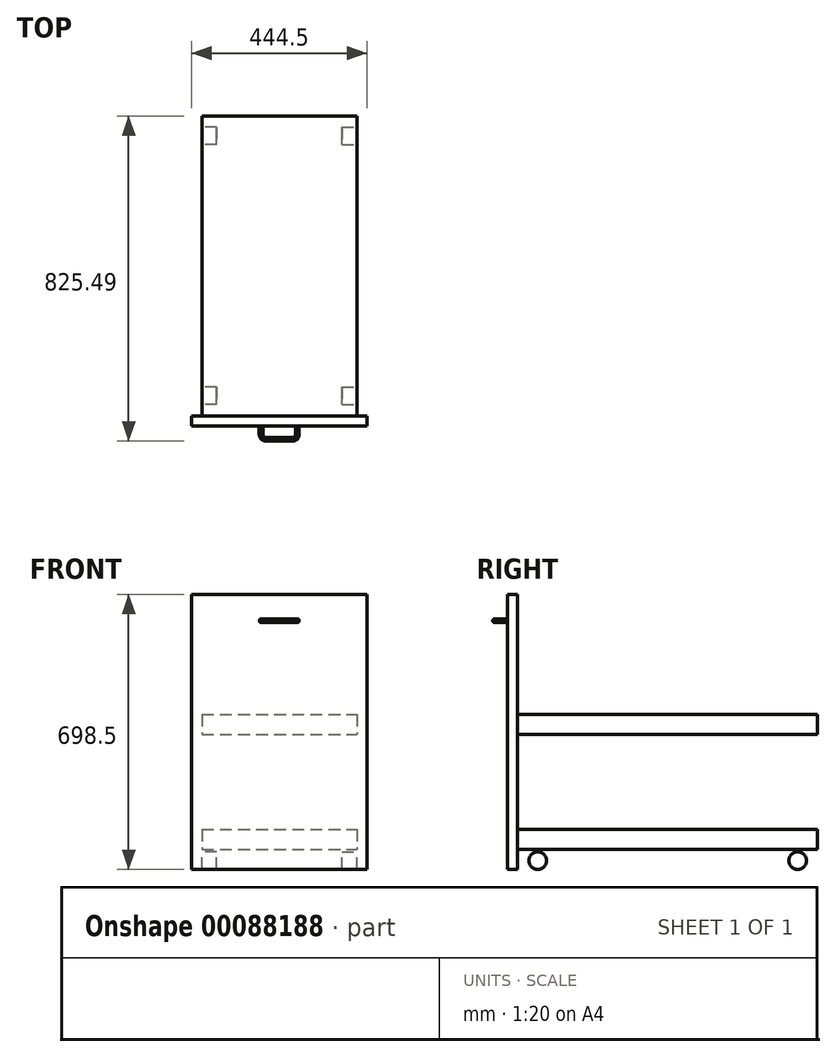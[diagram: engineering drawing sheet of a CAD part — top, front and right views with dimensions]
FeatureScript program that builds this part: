
annotation { "Feature Type Name" : "Feature", "Feature Type Description" : "" }
export const myFeature = defineFeature(function(context is Context, id is Id, definition is map)
    precondition{}
    {
        {
            var Q0;
            Q0=qCreatedBy(makeId("Front.planeOp"),FACE);
            var sketch = newSketch(context, id + "F0", { "sketchPlane" : qUnion([Q0])});
            skLineSegment(sketch, "E0.bottom", {"start": v(-222.25, 0) * mm, "end": v(222.25, 0) * mm});
            skLineSegment(sketch, "E0.top", {"start": v(-222.25, 698.5) * mm, "end": v(222.25, 698.5) * mm});
            skLineSegment(sketch, "E0.left", {"start": v(-222.25, 0) * mm, "end": v(-222.25, 698.5) * mm});
            skLineSegment(sketch, "E0.right", {"start": v(222.25, 0) * mm, "end": v(222.25, 698.5) * mm});
            skPoint(sketch, "E1", {"position": v(0, 0) * mm});
            skSolve(sketch);
        }
        {
            var Q0;
            Q0 = qSketchRegion(id + "F0", true);
            extrude(context, id + "F1", {"entities" : qUnion([Q0]), "depth" : 25.4 * mm});
        }
        {
            var Q0;
            Q0=makeQuery(id+"F1.opExtrude","CAP_FACE",FACE,{"disambiguationData":[OSD([sQuery(id+"F0.wireOp",EDGE,"E0.bottom"),sQuery(id+"F0.wireOp",EDGE,"E0.top"),sQuery(id+"F0.wireOp",EDGE,"E0.left"),sQuery(id+"F0.wireOp",EDGE,"E0.right")])],"isStart":true});
            var sketch = newSketch(context, id + "F2", { "sketchPlane" : qUnion([Q0])});
            skLineSegment(sketch, "E2.bottom", {"start": v(196.85, 393.7) * mm, "end": v(-196.85, 393.7) * mm});
            skLineSegment(sketch, "E2.top", {"start": v(196.85, 342.9) * mm, "end": v(-196.85, 342.9) * mm});
            skLineSegment(sketch, "E2.left", {"start": v(196.85, 393.7) * mm, "end": v(196.85, 342.9) * mm});
            skLineSegment(sketch, "E2.right", {"start": v(-196.85, 393.7) * mm, "end": v(-196.85, 342.9) * mm});
            skLineSegment(sketch, "E3.bottom", {"start": v(196.85, 101.6) * mm, "end": v(-196.85, 101.6) * mm});
            skLineSegment(sketch, "E3.top", {"start": v(196.85, 50.8) * mm, "end": v(-196.85, 50.8) * mm});
            skLineSegment(sketch, "E3.left", {"start": v(196.85, 101.6) * mm, "end": v(196.85, 50.8) * mm});
            skLineSegment(sketch, "E3.right", {"start": v(-196.85, 101.6) * mm, "end": v(-196.85, 50.8) * mm});
            skLineSegment(sketch, "E4", {"start": v(0, 698.5) * mm, "end": v(0, 393.7) * mm, "construction": true});
            skSolve(sketch);
        }
        {
            var Q0;
            Q0 = qSketchRegion(id + "F2", true);
            extrude(context, id + "F3", {"entities" : qUnion([Q0]), "operationType" : NewBodyOperationType.ADD, "depth" : 762 * mm});
        }
        {
            var Q0;
            Q0=makeQuery(id+"F3.opExtrude","SWEPT_FACE",FACE,{"disambiguationData":[OSD([sQuery(id+"F2.wireOp",EDGE,"E3.right")])]});
            var sketch = newSketch(context, id + "F4", { "sketchPlane" : qUnion([Q0])});
            skCircle(sketch, "E5", {"center": v(50.8, 22.22) * mm, "radius": 22.23 * mm});
            skCircle(sketch, "E6", {"center": v(711.2, 22.23) * mm, "radius": 22.23 * mm});
            skLineSegment(sketch, "E7", {"start": v(0, 0) * mm, "end": v(50.8, 0) * mm, "construction": true});
            skSolve(sketch);
        }
        {
            var Q0;
            Q0 = qSketchRegion(id + "F4", true);
            extrude(context, id + "F5", {"entities" : qUnion([Q0]), "oppositeDirection" : true, "depth" : 38.1 * mm});
        }
        {
            var Q0;
            Q0=makeQuery(id+"F5.opExtrude","SWEPT_BODY",BODY,{"disambiguationData":[OSD([sQuery(id+"F4.wireOp",EDGE,"E5")])]});
            var Q1;
            Q1=makeQuery(id+"F5.opExtrude","SWEPT_BODY",BODY,{"disambiguationData":[OSD([sQuery(id+"F4.wireOp",EDGE,"E6")])]});
            var Q2;
            Q2=qCreatedBy(makeId("Right.planeOp"),FACE);
            mirror(context, id + "F6", {"entities" : qUnion([Q0, Q1]), "mirrorPlane" : qUnion([Q2])});
        }
        {
            var Q0;
            Q0=qCreatedBy(makeId("Top.planeOp"),FACE);
            var sketch = newSketch(context, id + "F7", { "sketchPlane" : qUnion([Q0])});
            skLineSegment(sketch, "E8.bottom", {"start": v(-50.8, -25.4) * mm, "end": v(-41.28, -25.4) * mm});
            skLineSegment(sketch, "E8.top", {"start": v(-34.93, -63.5) * mm, "end": v(34.93, -63.5) * mm});
            skLineSegment(sketch, "E8.left", {"start": v(-50.8, -25.4) * mm, "end": v(-50.8, -47.62) * mm});
            skLineSegment(sketch, "E8.right", {"start": v(50.8, -25.4) * mm, "end": v(50.8, -47.62) * mm});
            skLineSegment(sketch, "E9.top", {"start": v(-34.93, -53.98) * mm, "end": v(34.93, -53.97) * mm});
            skLineSegment(sketch, "E9.left", {"start": v(-41.28, -25.4) * mm, "end": v(-41.28, -47.62) * mm});
            skLineSegment(sketch, "E9.right", {"start": v(41.28, -25.4) * mm, "end": v(41.28, -47.62) * mm});
            skLineSegment(sketch, "E10.trimOffspring", {"start": v(41.28, -25.4) * mm, "end": v(50.8, -25.4) * mm});
            skPoint(sketch, "E11", {"position": v(0, -53.98) * mm});
            skPoint(sketch, "E12.visualSharp", {"position": v(-41.27, -53.98) * mm});
            skArc(sketch, "E12.filletArc", {"start": v(-41.28, -47.62) * mm, "mid": v(-39.42, -52.12) * mm, "end": v(-34.93, -53.97) * mm});
            skPoint(sketch, "E13.visualSharp", {"position": v(41.27, -53.97) * mm});
            skArc(sketch, "E13.filletArc", {"start": v(34.93, -53.98) * mm, "mid": v(39.42, -52.12) * mm, "end": v(41.28, -47.62) * mm});
            skPoint(sketch, "E14.visualSharp", {"position": v(-50.8, -63.5) * mm});
            skArc(sketch, "E14.filletArc", {"start": v(-50.8, -47.63) * mm, "mid": v(-46.15, -58.85) * mm, "end": v(-34.93, -63.5) * mm});
            skPoint(sketch, "E15.visualSharp", {"position": v(50.8, -63.5) * mm});
            skArc(sketch, "E15.filletArc", {"start": v(34.93, -63.5) * mm, "mid": v(46.15, -58.85) * mm, "end": v(50.8, -47.62) * mm});
            skSolve(sketch);
        }
        {
            var Q0;
            Q0 = qSketchRegion(id + "F7", true);
            extrude(context, id + "F8", {"entities" : qUnion([Q0]), "depth" : 9.52 * mm});
        }
        {
            var Q0;
            Q0=makeQuery(id+"F8.opExtrude","SWEPT_BODY",BODY,{"disambiguationData":[OSD([sQuery(id+"F7.wireOp",EDGE,"E8.bottom"),sQuery(id+"F7.wireOp",EDGE,"E8.top"),sQuery(id+"F7.wireOp",EDGE,"E8.left"),sQuery(id+"F7.wireOp",EDGE,"E8.right"),sQuery(id+"F7.wireOp",EDGE,"E9.top"),sQuery(id+"F7.wireOp",EDGE,"E9.left"),sQuery(id+"F7.wireOp",EDGE,"E9.right"),sQuery(id+"F7.wireOp",EDGE,"E10.trimOffspring")])]});
            transform(context, id + "F9", {"entities" : qUnion([Q0]), "transformType" : TransformType.TRANSLATION_3D, "dx" : 0 * mm, "dy" : 0 * mm, "dz" : 627.17 * mm, "makeCopy" : false});
        }
        {
            var Q0;
            Q0=makeQuery(id+"F8.opExtrude","CAP_EDGE",EDGE,{"disambiguationData":[OSD([sQuery(id+"F7.wireOp",EDGE,"E9.left")])],"isStart":false});
            var Q1;
            Q1=makeQuery(id+"F8.opExtrude","CAP_EDGE",EDGE,{"disambiguationData":[OSD([sQuery(id+"F7.wireOp",EDGE,"E8.left")])],"isStart":false});
            var Q2;
            Q2=makeQuery(id+"F8.opExtrude","CAP_EDGE",EDGE,{"disambiguationData":[OSD([sQuery(id+"F7.wireOp",EDGE,"E9.left")])],"isStart":true});
            var Q3;
            Q3=makeQuery(id+"F8.opExtrude","CAP_EDGE",EDGE,{"disambiguationData":[OSD([sQuery(id+"F7.wireOp",EDGE,"E8.top")])],"isStart":true});
            fillet(context, id + "F10", {"entities" : qUnion([Q0, Q1, Q2, Q3]), "radius" : 5.08 * mm, "tangentPropagation" : true, "allowEdgeOverflow" : false});
        }
    });
